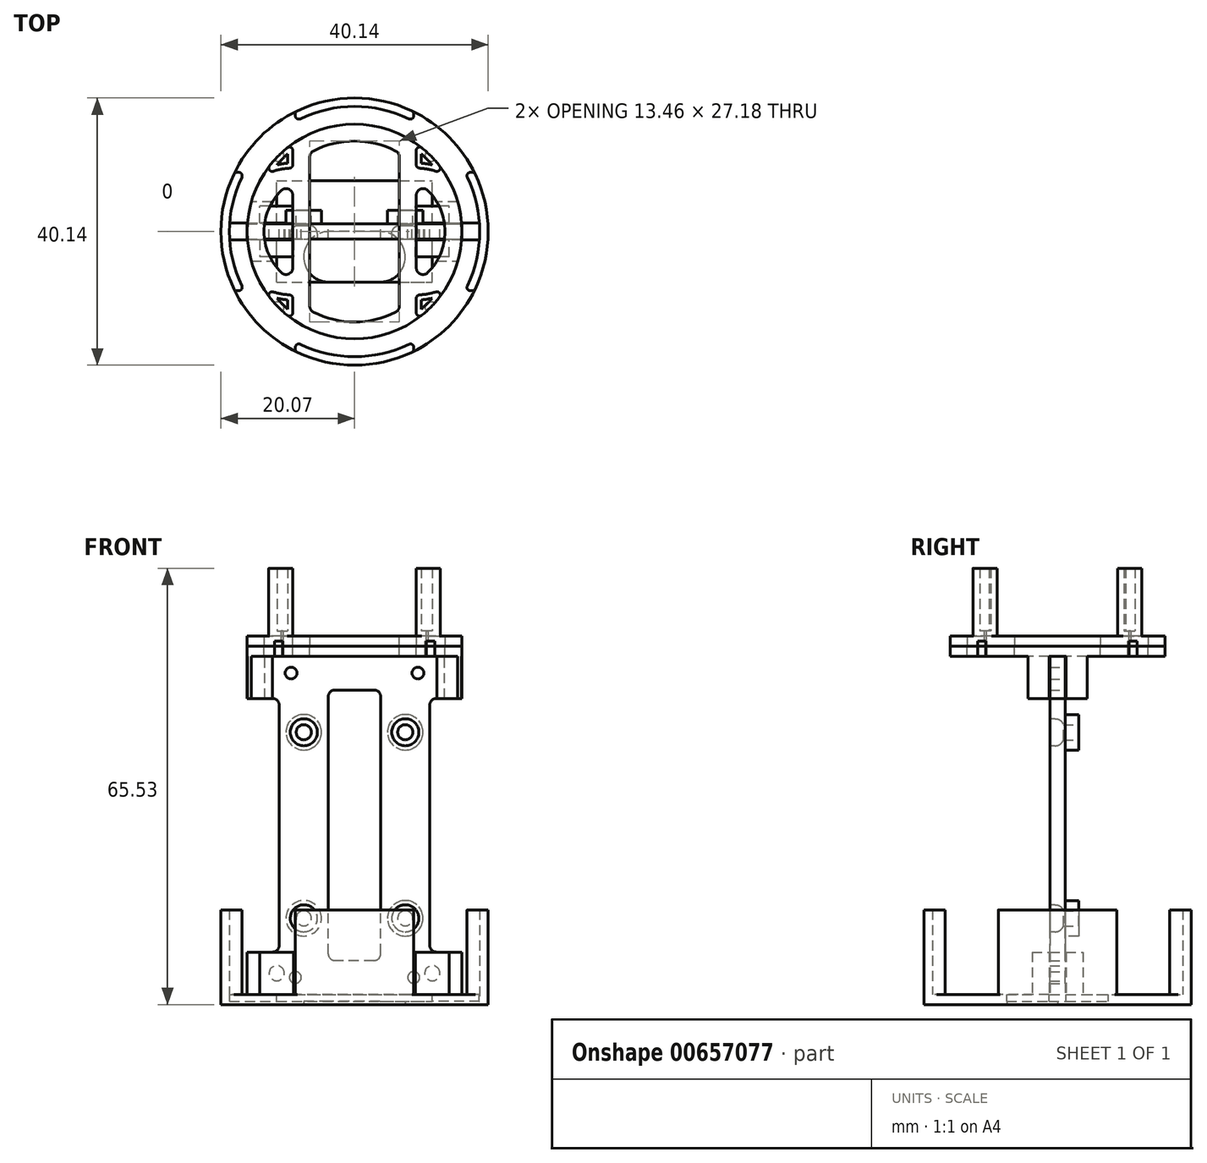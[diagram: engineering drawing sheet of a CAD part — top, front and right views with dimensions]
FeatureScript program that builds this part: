
annotation { "Feature Type Name" : "Feature", "Feature Type Description" : "" }
export const myFeature = defineFeature(function(context is Context, id is Id, definition is map)
    precondition{}
    {
        {
            var Q0;
            Q0=qCreatedBy(makeId("Top.planeOp"),FACE);
            var sketch = newSketch(context, id + "F0", { "sketchPlane" : qUnion([Q0])});
            skCircle(sketch, "E0", {"center": v(0, 0) * mm, "radius": 16.13 * mm});
            skSolve(sketch);
        }
        {
            var Q0;
            Q0=qSketchRegion(id+"F0",true);
            extrude(context, id + "F1", {"entities" : qUnion([Q0]), "depth" : 1.52 * mm, "offsetDistance" : 25.4 * mm});
        }
        {
            var Q0;
            Q0=makeQuery(id+"F1.opExtrude","CAP_FACE",FACE,{"disambiguationData":[OSD([sQuery(id+"F0.wireOp",EDGE,"E0")])],"isStart":false});
            var sketch = newSketch(context, id + "F2", { "sketchPlane" : qUnion([Q0])});
            skLineSegment(sketch, "E1.bottom", {"start": v(-9.27, 9.53) * mm, "end": v(9.27, 9.53) * mm, "construction": true});
            skLineSegment(sketch, "E1.top", {"start": v(-9.27, -9.53) * mm, "end": v(9.27, -9.53) * mm, "construction": true});
            skLineSegment(sketch, "E1.left", {"start": v(-9.27, 9.52) * mm, "end": v(-9.27, -9.53) * mm, "construction": true});
            skLineSegment(sketch, "E1.right", {"start": v(9.27, 9.53) * mm, "end": v(9.27, -9.53) * mm, "construction": true});
            skPoint(sketch, "E1.middle", {"position": v(0, 0) * mm});
            skArc(sketch, "E2", {"start": v(-9.27, 9.52) * mm, "mid": v(-11.6, 9.24) * mm, "end": v(-13.77, 8.4) * mm});
            skArc(sketch, "E3", {"start": v(9.27, -9.52) * mm, "mid": v(11.6, -9.24) * mm, "end": v(13.77, -8.4) * mm});
            skArc(sketch, "E4", {"start": v(-13.77, 8.4) * mm, "mid": v(-18.8, 0) * mm, "end": v(-13.77, -8.4) * mm, "construction": true});
            skArc(sketch, "E5", {"start": v(-13.77, 8.4) * mm, "mid": v(-16.13, 0) * mm, "end": v(-13.77, -8.4) * mm, "construction": true});
            skArc(sketch, "E6", {"start": v(-13.77, -8.4) * mm, "mid": v(0, -16.13) * mm, "end": v(13.77, -8.4) * mm});
            skArc(sketch, "E7", {"start": v(-13.77, -8.4) * mm, "mid": v(-11.6, -9.24) * mm, "end": v(-9.27, -9.53) * mm});
            skArc(sketch, "E8", {"start": v(13.77, 8.4) * mm, "mid": v(11.6, 9.24) * mm, "end": v(9.27, 9.53) * mm});
            skLineSegment(sketch, "E9", {"start": v(13.77, -8.4) * mm, "end": v(13.77, -8.4) * mm});
            skArc(sketch, "E10", {"start": v(13.77, -8.4) * mm, "mid": v(18.8, 0) * mm, "end": v(13.77, 8.4) * mm, "construction": true});
            skLineSegment(sketch, "E11", {"start": v(13.77, 8.4) * mm, "end": v(13.77, 8.4) * mm});
            skArc(sketch, "E12", {"start": v(13.77, 8.4) * mm, "mid": v(0, 16.13) * mm, "end": v(-13.77, 8.4) * mm});
            skArc(sketch, "E13", {"start": v(13.77, -8.4) * mm, "mid": v(16.13, 0) * mm, "end": v(13.77, 8.4) * mm, "construction": true});
            skLineSegment(sketch, "E14", {"start": v(-9.27, -9.53) * mm, "end": v(-9.27, -13.2) * mm});
            skLineSegment(sketch, "E15", {"start": v(9.27, -9.53) * mm, "end": v(9.27, -13.2) * mm});
            skLineSegment(sketch, "E16", {"start": v(9.27, 9.53) * mm, "end": v(9.27, 13.2) * mm});
            skLineSegment(sketch, "E17", {"start": v(-9.27, 9.53) * mm, "end": v(-9.27, 13.2) * mm});
            skArc(sketch, "E18", {"start": v(9.27, 13.2) * mm, "mid": v(0, 16.13) * mm, "end": v(-9.27, 13.2) * mm});
            skArc(sketch, "E19", {"start": v(-9.27, -13.2) * mm, "mid": v(0, -16.13) * mm, "end": v(9.27, -13.2) * mm});
            skSolve(sketch);
        }
        {
            var Q0;
            Q0=qSketchRegion(id+"F2",true);
            extrude(context, id + "F3", {"entities" : qUnion([Q0]), "operationType" : NewBodyOperationType.ADD, "depth" : 10.16 * mm, "offsetDistance" : 25.4 * mm});
        }
        {
            var Q0;
            Q0=makeQuery(id+"F3.opExtrude","SWEPT_EDGE",EDGE,{"disambiguationData":[OSD([sQuery(id+"F0.wireOp",EDGE,"E0"),sQuery(id+"F2.wireOp",EDGE,"E2"),sQuery(id+"F2.wireOp",EDGE,"E12")])]});
            var Q1;
            Q1=makeQuery(id+"F3.opExtrude","SWEPT_EDGE",EDGE,{"disambiguationData":[OSD([sQuery(id+"F0.wireOp",EDGE,"E0"),sQuery(id+"F2.wireOp",EDGE,"E6"),sQuery(id+"F2.wireOp",EDGE,"E7")])]});
            var Q2;
            Q2=makeQuery(id+"F3.opExtrude","SWEPT_EDGE",EDGE,{"disambiguationData":[OSD([sQuery(id+"F0.wireOp",EDGE,"E0"),sQuery(id+"F2.wireOp",EDGE,"E8"),sQuery(id+"F2.wireOp",EDGE,"E12")])]});
            var Q3;
            Q3=makeQuery(id+"F3.opExtrude","SWEPT_EDGE",EDGE,{"disambiguationData":[OSD([sQuery(id+"F0.wireOp",EDGE,"E0"),sQuery(id+"F2.wireOp",EDGE,"E3"),sQuery(id+"F2.wireOp",EDGE,"E6")])]});
            var Q4;
            Q4=makeQuery(id+"F3.opExtrude","SWEPT_EDGE",EDGE,{"disambiguationData":[OSD([sQuery(id+"F2.wireOp",EDGE,"E6"),sQuery(id+"F2.wireOp",EDGE,"E14"),sQuery(id+"F2.wireOp",EDGE,"E19")])]});
            var Q5;
            Q5=makeQuery(id+"F3.opExtrude","SWEPT_EDGE",EDGE,{"disambiguationData":[OSD([sQuery(id+"F0.wireOp",EDGE,"RRU1Pf1V-DoVO-Xhje-gmtz-4FpblWX3eckG.bottom"),sQuery(id+"F0.wireOp",EDGE,"RRU1Pf1V-DoVO-Xhje-gmtz-4FpblWX3eckG.left"),sQuery(id+"F2.wireOp",EDGE,"E7"),sQuery(id+"F2.wireOp",EDGE,"E14")])]});
            var Q6;
            Q6=makeQuery(id+"F3.opExtrude","SWEPT_EDGE",EDGE,{"disambiguationData":[OSD([sQuery(id+"F0.wireOp",EDGE,"RRU1Pf1V-DoVO-Xhje-gmtz-4FpblWX3eckG.top"),sQuery(id+"F0.wireOp",EDGE,"RRU1Pf1V-DoVO-Xhje-gmtz-4FpblWX3eckG.left"),sQuery(id+"F2.wireOp",EDGE,"E2"),sQuery(id+"F2.wireOp",EDGE,"E17")])]});
            var Q7;
            Q7=makeQuery(id+"F3.opExtrude","SWEPT_EDGE",EDGE,{"disambiguationData":[OSD([sQuery(id+"F2.wireOp",EDGE,"E12"),sQuery(id+"F2.wireOp",EDGE,"E17"),sQuery(id+"F2.wireOp",EDGE,"E18")])]});
            var Q8;
            Q8=makeQuery(id+"F3.opExtrude","SWEPT_EDGE",EDGE,{"disambiguationData":[OSD([sQuery(id+"F2.wireOp",EDGE,"E12"),sQuery(id+"F2.wireOp",EDGE,"E16"),sQuery(id+"F2.wireOp",EDGE,"E18")])]});
            var Q9;
            Q9=makeQuery(id+"F3.opExtrude","SWEPT_EDGE",EDGE,{"disambiguationData":[OSD([sQuery(id+"F2.wireOp",EDGE,"E6"),sQuery(id+"F2.wireOp",EDGE,"E15"),sQuery(id+"F2.wireOp",EDGE,"E19")])]});
            var Q10;
            Q10=makeQuery(id+"F3.opExtrude","SWEPT_EDGE",EDGE,{"disambiguationData":[OSD([sQuery(id+"F0.wireOp",EDGE,"RRU1Pf1V-DoVO-Xhje-gmtz-4FpblWX3eckG.top"),sQuery(id+"F0.wireOp",EDGE,"RRU1Pf1V-DoVO-Xhje-gmtz-4FpblWX3eckG.right"),sQuery(id+"F2.wireOp",EDGE,"E8"),sQuery(id+"F2.wireOp",EDGE,"E16")])]});
            var Q11;
            Q11=makeQuery(id+"F3.opExtrude","SWEPT_EDGE",EDGE,{"disambiguationData":[OSD([sQuery(id+"F0.wireOp",EDGE,"RRU1Pf1V-DoVO-Xhje-gmtz-4FpblWX3eckG.bottom"),sQuery(id+"F0.wireOp",EDGE,"RRU1Pf1V-DoVO-Xhje-gmtz-4FpblWX3eckG.right"),sQuery(id+"F2.wireOp",EDGE,"E3"),sQuery(id+"F2.wireOp",EDGE,"E15")])]});
            fillet(context, id + "F4", {"entities" : qUnion([Q0, Q1, Q2, Q3, Q4, Q5, Q6, Q7, Q8, Q9, Q10, Q11]), "radius" : 0.5 * mm, "tangentPropagation" : true, "allowEdgeOverflow" : false});
        }
        {
            var Q0;
            Q0=makeQuery(id+"F3.opExtrude","CAP_FACE",FACE,{"disambiguationData":[OSD([sQuery(id+"F2.wireOp",EDGE,"E1.bottom"),sQuery(id+"F2.wireOp",EDGE,"E2"),sQuery(id+"F2.wireOp",EDGE,"E8"),sQuery(id+"F2.wireOp",EDGE,"E12")])],"isStart":false});
            var Q1;
            Q1=makeQuery(id+"F3.opExtrude","CAP_FACE",FACE,{"disambiguationData":[OSD([sQuery(id+"F2.wireOp",EDGE,"E1.top"),sQuery(id+"F2.wireOp",EDGE,"E3"),sQuery(id+"F2.wireOp",EDGE,"E6"),sQuery(id+"F2.wireOp",EDGE,"E7")])],"isStart":false});
            shell(context, id + "F5", {"entities" : qUnion([Q0, Q1]), "thickness" : 0.76 * mm});
        }
        {
            var Q0;
            Q0=makeQuery(id+"F1.opExtrude","CAP_FACE",FACE,{"disambiguationData":[OSD([sQuery(id+"F0.wireOp",EDGE,"E0")])],"isStart":true});
            var sketch = newSketch(context, id + "F6", { "sketchPlane" : qUnion([Q0])});
            skLineSegment(sketch, "E20.bottom", {"start": v(6.73, -11.8) * mm, "end": v(-6.73, -11.8) * mm, "construction": true});
            skLineSegment(sketch, "E20.top", {"start": v(6.73, 11.8) * mm, "end": v(-6.73, 11.8) * mm, "construction": true});
            skLineSegment(sketch, "E20.left", {"start": v(6.73, -11.8) * mm, "end": v(6.73, 11.8) * mm});
            skLineSegment(sketch, "E20.right", {"start": v(-6.73, -11.8) * mm, "end": v(-6.73, 11.8) * mm});
            skPoint(sketch, "E20.middle", {"position": v(0, 0) * mm});
            skArc(sketch, "E21", {"start": v(-6.73, -11.8) * mm, "mid": v(0, -13.59) * mm, "end": v(6.73, -11.8) * mm});
            skArc(sketch, "E22", {"start": v(6.73, 11.8) * mm, "mid": v(0, 13.59) * mm, "end": v(-6.73, 11.8) * mm});
            skLineSegment(sketch, "E23", {"start": v(0, -13.59) * mm, "end": v(0, -16.13) * mm, "construction": true});
            skLineSegment(sketch, "E24", {"start": v(6.73, -11.8) * mm, "end": v(9.27, -11.8) * mm, "construction": true});
            skLineSegment(sketch, "E25", {"start": v(9.27, -7.48) * mm, "end": v(9.27, 7.48) * mm});
            skPoint(sketch, "E26", {"position": v(9.27, 0) * mm});
            skArc(sketch, "E27", {"start": v(9.27, -7.48) * mm, "mid": v(13.59, 0) * mm, "end": v(9.27, 7.48) * mm});
            skLineSegment(sketch, "E28", {"start": v(13.59, 0) * mm, "end": v(16.13, 0) * mm, "construction": true});
            skLineSegment(sketch, "E29", {"start": v(9.27, -7.48) * mm, "end": v(9.27, -10.02) * mm, "construction": true});
            skLineSegment(sketch, "E30", {"start": v(-9.27, -7.48) * mm, "end": v(-9.27, 7.48) * mm});
            skArc(sketch, "E31", {"start": v(-9.27, 7.48) * mm, "mid": v(-13.59, 0) * mm, "end": v(-9.27, -7.48) * mm});
            skLineSegment(sketch, "E32", {"start": v(-13.59, 0) * mm, "end": v(-16.13, 0) * mm, "construction": true});
            skSolve(sketch);
        }
        {
            var Q0;
            Q0=qSketchRegion(id+"F6",true);
            var Q1;
            Q1=makeQuery(id+"F1.opExtrude","CAP_FACE",FACE,{"disambiguationData":[OSD([sQuery(id+"F0.wireOp",EDGE,"E0")])],"isStart":false});
            extrude(context, id + "F7", {"entities" : qUnion([Q0]), "operationType" : NewBodyOperationType.REMOVE, "endBound" : BoundingType.UP_TO_SURFACE, "oppositeDirection" : true, "depth" : 25.4 * mm, "endBoundEntityFace" : qUnion([Q1]), "offsetDistance" : 25.4 * mm});
        }
        {
            var Q0;
            Q0=makeQuery(id+"F3.opExtrude","CAP_EDGE",EDGE,{"disambiguationData":[OSD([sQuery(id+"F2.wireOp",EDGE,"E2")])],"isStart":true});
            var Q1;
            Q1=makeQuery(id+"F3.opExtrude","CAP_EDGE",EDGE,{"disambiguationData":[OSD([sQuery(id+"F2.wireOp",EDGE,"E7")])],"isStart":true});
            var Q2;
            Q2=makeQuery(id+"F3.opExtrude","CAP_EDGE",EDGE,{"disambiguationData":[OSD([sQuery(id+"F2.wireOp",EDGE,"E3")])],"isStart":true});
            var Q3;
            Q3=makeQuery(id+"F3.opExtrude","CAP_EDGE",EDGE,{"disambiguationData":[OSD([sQuery(id+"F2.wireOp",EDGE,"E8")])],"isStart":true});
            var Q4;
            {var subQ0=sQuery(id+"F6.wireOp",EDGE,"E31");var subQ1=sQuery(id+"F6.wireOp",EDGE,"E30");Q4=makeQuery(id+"F7.boolean.opBoolean","COPY",EDGE,{"derivedFrom":makeQuery(id+"F7.opExtrude","SWEPT_EDGE",EDGE,{"disambiguationData":[OSD([subQ1,subQ0]),TDD([makeQuery(id+"F6.imprint","INTERSECT",VERTEX,{"disambiguationData":[OD(0.0)],"derivedFrom":[subQ1,subQ0]})])]})});}
            var Q5;
            Q5=makeQuery(id+"F7.boolean.opBoolean","COPY",EDGE,{"derivedFrom":makeQuery(id+"F7.opExtrude","SWEPT_EDGE",EDGE,{"disambiguationData":[OSD([sQuery(id+"F6.wireOp",EDGE,"E20.right"),sQuery(id+"F6.wireOp",EDGE,"E21")])]})});
            var Q6;
            Q6=makeQuery(id+"F7.boolean.opBoolean","COPY",EDGE,{"derivedFrom":makeQuery(id+"F7.opExtrude","SWEPT_EDGE",EDGE,{"disambiguationData":[OSD([sQuery(id+"F6.wireOp",EDGE,"E20.left"),sQuery(id+"F6.wireOp",EDGE,"E21")])]})});
            var Q7;
            {var subQ0=sQuery(id+"F6.wireOp",EDGE,"E31");var subQ1=sQuery(id+"F6.wireOp",EDGE,"E30");Q7=makeQuery(id+"F7.boolean.opBoolean","COPY",EDGE,{"derivedFrom":makeQuery(id+"F7.opExtrude","SWEPT_EDGE",EDGE,{"disambiguationData":[OSD([subQ1,subQ0]),TDD([makeQuery(id+"F6.imprint","INTERSECT",VERTEX,{"disambiguationData":[OD(1.0)],"derivedFrom":[subQ1,subQ0]})])]})});}
            var Q8;
            Q8=makeQuery(id+"F7.boolean.opBoolean","COPY",EDGE,{"derivedFrom":makeQuery(id+"F7.opExtrude","SWEPT_EDGE",EDGE,{"disambiguationData":[OSD([sQuery(id+"F6.wireOp",EDGE,"E20.left"),sQuery(id+"F6.wireOp",EDGE,"E22")])]})});
            var Q9;
            {var subQ0=sQuery(id+"F6.wireOp",EDGE,"E27");var subQ1=sQuery(id+"F6.wireOp",EDGE,"E25");Q9=makeQuery(id+"F7.boolean.opBoolean","COPY",EDGE,{"derivedFrom":makeQuery(id+"F7.opExtrude","SWEPT_EDGE",EDGE,{"disambiguationData":[OSD([subQ1,subQ0]),TDD([makeQuery(id+"F6.imprint","INTERSECT",VERTEX,{"disambiguationData":[OD(1.0)],"derivedFrom":[subQ1,subQ0]})])]})});}
            var Q10;
            Q10=makeQuery(id+"F7.boolean.opBoolean","COPY",EDGE,{"derivedFrom":makeQuery(id+"F7.opExtrude","SWEPT_EDGE",EDGE,{"disambiguationData":[OSD([sQuery(id+"F6.wireOp",EDGE,"E20.right"),sQuery(id+"F6.wireOp",EDGE,"E22")])]})});
            var Q11;
            {var subQ0=sQuery(id+"F6.wireOp",EDGE,"E27");var subQ1=sQuery(id+"F6.wireOp",EDGE,"E25");Q11=makeQuery(id+"F7.boolean.opBoolean","COPY",EDGE,{"derivedFrom":makeQuery(id+"F7.opExtrude","SWEPT_EDGE",EDGE,{"disambiguationData":[OSD([subQ1,subQ0]),TDD([makeQuery(id+"F6.imprint","INTERSECT",VERTEX,{"disambiguationData":[OD(0.0)],"derivedFrom":[subQ1,subQ0]})])]})});}
            fillet(context, id + "F8", {"entities" : qUnion([Q0, Q1, Q2, Q3, Q4, Q5, Q6, Q7, Q8, Q9, Q10, Q11]), "radius" : 1.02 * mm, "tangentPropagation" : true, "allowEdgeOverflow" : false});
        }
        {
            var Q0;
            Q0=makeQuery(id+"F5.opShell","OFFSET_FACE",FACE,{"disambiguationData":[OSD([sQuery(id+"F0.wireOp",EDGE,"E0")]),OD(0.0)]});
            var sketch = newSketch(context, id + "F9", { "sketchPlane" : qUnion([Q0])});
            skCircle(sketch, "E33", {"center": v(-11.5, 11.46) * mm, "radius": 0.89 * mm});
            skLineSegment(sketch, "E34.bottom", {"start": v(-11.5, 11.46) * mm, "end": v(11.5, 11.46) * mm, "construction": true});
            skLineSegment(sketch, "E34.top", {"start": v(-11.5, -11.46) * mm, "end": v(11.5, -11.46) * mm, "construction": true});
            skLineSegment(sketch, "E34.left", {"start": v(-11.5, 11.46) * mm, "end": v(-11.5, -11.46) * mm, "construction": true});
            skLineSegment(sketch, "E34.right", {"start": v(11.5, 11.46) * mm, "end": v(11.5, -11.46) * mm, "construction": true});
            skPoint(sketch, "E34.middle", {"position": v(0, 0) * mm});
            skCircle(sketch, "E35", {"center": v(11.5, 11.46) * mm, "radius": 0.89 * mm});
            skCircle(sketch, "E36", {"center": v(11.5, -11.46) * mm, "radius": 0.89 * mm});
            skCircle(sketch, "E37", {"center": v(-11.5, -11.46) * mm, "radius": 0.89 * mm});
            skSolve(sketch);
        }
        {
            var Q0;
            Q0=qSketchRegion(id+"F9",true);
            var Q1;
            Q1=makeQuery(id+"F1.opExtrude","CAP_FACE",FACE,{"disambiguationData":[OSD([sQuery(id+"F0.wireOp",EDGE,"E0")])],"isStart":true});
            extrude(context, id + "F10", {"entities" : qUnion([Q0]), "operationType" : NewBodyOperationType.REMOVE, "endBound" : BoundingType.UP_TO_SURFACE, "oppositeDirection" : true, "depth" : 25.4 * mm, "endBoundEntityFace" : qUnion([Q1]), "offsetDistance" : 25.4 * mm});
        }
        {
            var Q0;
            Q0=makeQuery(id+"F5.opShell","OFFSET_FACE",FACE,{"disambiguationData":[OSD([sQuery(id+"F0.wireOp",EDGE,"E0")]),OD(2.0)]});
            var Q1;
            Q1=makeQuery(id+"F5.opShell","OFFSET_FACE",FACE,{"disambiguationData":[OSD([sQuery(id+"F0.wireOp",EDGE,"E0")]),OD(1.0)]});
            var Q2;
            Q2=makeQuery(id+"F5.opShell","OFFSET_FACE",FACE,{"disambiguationData":[OSD([sQuery(id+"F0.wireOp",EDGE,"E0")]),OD(3.0)]});
            var Q3;
            Q3=makeQuery(id+"F5.opShell","OFFSET_FACE",FACE,{"disambiguationData":[OSD([sQuery(id+"F0.wireOp",EDGE,"E0")]),OD(0.0)]});
            extrude(context, id + "F11", {"entities" : qUnion([Q0, Q1, Q2, Q3]), "operationType" : NewBodyOperationType.ADD, "depth" : 1.52 * mm, "offsetDistance" : 25.4 * mm});
        }
        {
            var Q0;
            Q0=makeQuery(id+"F1.opExtrude","CAP_FACE",FACE,{"disambiguationData":[OSD([sQuery(id+"F0.wireOp",EDGE,"E0")])],"isStart":true});
            extrude(context, id + "F12", {"entities" : qUnion([Q0]), "depth" : 7.87 * mm, "offsetDistance" : 25.4 * mm});
        }
        {
            var Q0;
            Q0=makeQuery(id+"F12.opExtrude","CAP_FACE",FACE,{"disambiguationData":[OSD([sQuery(id+"F0.wireOp",EDGE,"E0")])],"isStart":false});
            var sketch = newSketch(context, id + "F13", { "sketchPlane" : qUnion([Q0])});
            skArc(sketch, "E38", {"start": v(-15.5, 4.44) * mm, "mid": v(-15.87, 2.87) * mm, "end": v(-16.08, 1.27) * mm, "construction": true});
            skArc(sketch, "E39", {"start": v(-15.5, -4.45) * mm, "mid": v(0, -16.13) * mm, "end": v(15.5, -4.45) * mm});
            skArc(sketch, "E40", {"start": v(15.5, -4.44) * mm, "mid": v(15.87, -2.87) * mm, "end": v(16.08, -1.27) * mm, "construction": true});
            skArc(sketch, "E41", {"start": v(15.5, 4.45) * mm, "mid": v(0, 16.13) * mm, "end": v(-15.5, 4.45) * mm});
            skLineSegment(sketch, "E42", {"start": v(-15.5, 4.45) * mm, "end": v(-9.27, 4.45) * mm});
            skLineSegment(sketch, "E43", {"start": v(15.5, -4.45) * mm, "end": v(9.27, -4.45) * mm});
            skArc(sketch, "E44", {"start": v(-16.08, 1.27) * mm, "mid": v(-16.13, 0) * mm, "end": v(-16.08, -1.27) * mm});
            skArc(sketch, "E45", {"start": v(-16.08, -1.27) * mm, "mid": v(-15.87, -2.87) * mm, "end": v(-15.5, -4.44) * mm, "construction": true});
            skArc(sketch, "E46", {"start": v(16.08, -1.27) * mm, "mid": v(16.13, 0) * mm, "end": v(16.08, 1.27) * mm});
            skArc(sketch, "E47", {"start": v(16.08, 1.27) * mm, "mid": v(15.87, 2.87) * mm, "end": v(15.5, 4.44) * mm, "construction": true});
            skLineSegment(sketch, "E48", {"start": v(16.08, 1.27) * mm, "end": v(9.27, 1.27) * mm});
            skLineSegment(sketch, "E49", {"start": v(-16.08, -1.27) * mm, "end": v(-9.27, -1.27) * mm});
            skLineSegment(sketch, "E50", {"start": v(-9.27, 4.45) * mm, "end": v(9.27, 4.45) * mm, "construction": true});
            skLineSegment(sketch, "E51", {"start": v(-9.27, 1.27) * mm, "end": v(-16.08, 1.27) * mm});
            skLineSegment(sketch, "E52", {"start": v(-9.27, -1.27) * mm, "end": v(9.27, -1.27) * mm, "construction": true});
            skLineSegment(sketch, "E53", {"start": v(-9.27, -4.45) * mm, "end": v(-15.5, -4.45) * mm});
            skLineSegment(sketch, "E54", {"start": v(9.27, -4.45) * mm, "end": v(-9.27, -4.45) * mm, "construction": true});
            skLineSegment(sketch, "E55", {"start": v(9.27, -1.27) * mm, "end": v(16.08, -1.27) * mm});
            skLineSegment(sketch, "E56", {"start": v(9.27, 1.27) * mm, "end": v(-9.27, 1.27) * mm, "construction": true});
            skLineSegment(sketch, "E57", {"start": v(9.27, 4.45) * mm, "end": v(15.5, 4.45) * mm});
            skLineSegment(sketch, "E58", {"start": v(0, 1.27) * mm, "end": v(0, -1.27) * mm, "construction": true});
            skLineSegment(sketch, "E59", {"start": v(0, 4.45) * mm, "end": v(0, -4.45) * mm, "construction": true});
            skLineSegment(sketch, "E60", {"start": v(-9.27, 4.45) * mm, "end": v(-9.27, 1.27) * mm});
            skLineSegment(sketch, "E61", {"start": v(-9.27, -1.27) * mm, "end": v(-9.27, -4.45) * mm});
            skLineSegment(sketch, "E62", {"start": v(9.27, -4.45) * mm, "end": v(9.27, -1.27) * mm});
            skLineSegment(sketch, "E63", {"start": v(9.27, 1.27) * mm, "end": v(9.27, 4.45) * mm});
            skSolve(sketch);
        }
        {
            var Q0;
            Q0=qSketchRegion(id+"F13",true);
            extrude(context, id + "F14", {"entities" : qUnion([Q0]), "operationType" : NewBodyOperationType.REMOVE, "oppositeDirection" : true, "depth" : 6.35 * mm, "offsetDistance" : 25.4 * mm});
        }
        {
            var Q0;
            Q0=qCreatedBy(makeId("Front.planeOp"),FACE);
            var sketch = newSketch(context, id + "F15", { "sketchPlane" : qUnion([Q0])});
            skLineSegment(sketch, "E64.bottom", {"start": v(-7.62, -40.9) * mm, "end": v(7.62, -40.9) * mm, "construction": true});
            skLineSegment(sketch, "E64.top", {"start": v(-7.62, -12.95) * mm, "end": v(7.62, -12.95) * mm, "construction": true});
            skLineSegment(sketch, "E64.left", {"start": v(-7.62, -40.9) * mm, "end": v(-7.62, -12.95) * mm, "construction": true});
            skLineSegment(sketch, "E64.right", {"start": v(7.62, -40.9) * mm, "end": v(7.62, -12.95) * mm, "construction": true});
            skPoint(sketch, "E64.middle", {"position": v(0, -26.92) * mm});
            skCircle(sketch, "E65", {"center": v(-7.62, -40.9) * mm, "radius": 1.14 * mm});
            skCircle(sketch, "E66", {"center": v(-7.62, -12.95) * mm, "radius": 1.14 * mm});
            skCircle(sketch, "E67", {"center": v(7.62, -12.95) * mm, "radius": 1.14 * mm});
            skCircle(sketch, "E68", {"center": v(7.62, -40.9) * mm, "radius": 1.14 * mm});
            skLineSegment(sketch, "E69", {"start": v(-8.89, -49.78) * mm, "end": v(8.89, -49.78) * mm, "construction": true});
            skLineSegment(sketch, "E70", {"start": v(-9.53, -4.06) * mm, "end": v(9.53, -4.06) * mm, "construction": true});
            skPoint(sketch, "E71", {"position": v(0, -49.78) * mm});
            skPoint(sketch, "E72", {"position": v(0, -4.06) * mm});
            skLineSegment(sketch, "E73", {"start": v(0, -49.78) * mm, "end": v(0, -4.06) * mm, "construction": true});
            skCircle(sketch, "E74", {"center": v(-8.89, -49.78) * mm, "radius": 0.89 * mm});
            skCircle(sketch, "E75", {"center": v(8.89, -49.78) * mm, "radius": 0.89 * mm});
            skCircle(sketch, "E76", {"center": v(9.53, -4.06) * mm, "radius": 0.89 * mm});
            skCircle(sketch, "E77", {"center": v(-9.53, -4.06) * mm, "radius": 0.89 * mm});
            skLineSegment(sketch, "E78", {"start": v(-16.13, -52.32) * mm, "end": v(16.13, -52.32) * mm});
            skPoint(sketch, "E79", {"position": v(0, -52.32) * mm});
            skLineSegment(sketch, "E80", {"start": v(-16.13, -1.52) * mm, "end": v(16.13, -1.52) * mm});
            skLineSegment(sketch, "E81", {"start": v(9.52, -4.06) * mm, "end": v(9.52, -1.52) * mm, "construction": true});
            skLineSegment(sketch, "E82", {"start": v(8.9, -49.78) * mm, "end": v(8.9, -52.32) * mm, "construction": true});
            skLineSegment(sketch, "E83", {"start": v(-16.13, -1.52) * mm, "end": v(-16.13, -7.87) * mm});
            skLineSegment(sketch, "E84", {"start": v(-16.13, -7.87) * mm, "end": v(-11.3, -7.87) * mm});
            skLineSegment(sketch, "E85", {"start": v(-11.3, -7.87) * mm, "end": v(-11.3, -45.97) * mm});
            skLineSegment(sketch, "E86", {"start": v(-11.3, -45.97) * mm, "end": v(-16.13, -45.97) * mm});
            skLineSegment(sketch, "E87", {"start": v(-16.13, -45.97) * mm, "end": v(-16.13, -52.32) * mm});
            skLineSegment(sketch, "E88", {"start": v(16.13, -1.52) * mm, "end": v(16.13, -7.87) * mm});
            skLineSegment(sketch, "E89", {"start": v(16.13, -7.87) * mm, "end": v(11.3, -7.87) * mm});
            skLineSegment(sketch, "E90", {"start": v(11.3, -7.87) * mm, "end": v(11.3, -45.97) * mm});
            skLineSegment(sketch, "E91", {"start": v(11.3, -45.97) * mm, "end": v(16.13, -45.97) * mm});
            skLineSegment(sketch, "E92", {"start": v(16.13, -45.97) * mm, "end": v(16.13, -52.32) * mm});
            skLineSegment(sketch, "E93", {"start": v(-8.76, -40.9) * mm, "end": v(-11.3, -40.9) * mm, "construction": true});
            skLineSegment(sketch, "E94.bottom", {"start": v(3.94, -47.24) * mm, "end": v(-3.94, -47.24) * mm});
            skLineSegment(sketch, "E94.top", {"start": v(3.94, -6.6) * mm, "end": v(-3.94, -6.6) * mm});
            skLineSegment(sketch, "E94.left", {"start": v(3.94, -47.24) * mm, "end": v(3.94, -6.6) * mm});
            skLineSegment(sketch, "E94.right", {"start": v(-3.94, -47.24) * mm, "end": v(-3.94, -6.6) * mm});
            skLineSegment(sketch, "E95", {"start": v(-6.48, -40.9) * mm, "end": v(-3.94, -40.9) * mm, "construction": true});
            skLineSegment(sketch, "E96", {"start": v(0, -49.78) * mm, "end": v(0, -47.24) * mm, "construction": true});
            skCircle(sketch, "E97", {"center": v(-11.68, -49.15) * mm, "radius": 1.14 * mm});
            skPoint(sketch, "E97.centerSnap0", {"position": v(-16.13, -49.15) * mm});
            skCircle(sketch, "E98", {"center": v(11.68, -49.15) * mm, "radius": 1.14 * mm});
            skPoint(sketch, "E98.centerSnap0", {"position": v(16.13, -49.15) * mm});
            skLineSegment(sketch, "E99", {"start": v(-11.68, -49.15) * mm, "end": v(-16.13, -49.15) * mm, "construction": true});
            skLineSegment(sketch, "E100", {"start": v(11.68, -49.15) * mm, "end": v(16.13, -49.15) * mm, "construction": true});
            skSolve(sketch);
        }
        {
            var Q0;
            Q0=qSketchRegion(id+"F15",true);
            extrude(context, id + "F16", {"entities" : qUnion([Q0]), "endBound" : BoundingType.SYMMETRIC, "depth" : 2.3 * mm, "offsetDistance" : 25.4 * mm});
        }
        {
            var Q0;
            Q0=makeQuery(id+"F16.opExtrude","CAP_FACE",FACE,{"disambiguationData":[OSD([sQuery(id+"F15.wireOp",EDGE,"E65"),sQuery(id+"F15.wireOp",EDGE,"E66"),sQuery(id+"F15.wireOp",EDGE,"E67"),sQuery(id+"F15.wireOp",EDGE,"E68"),sQuery(id+"F15.wireOp",EDGE,"E74"),sQuery(id+"F15.wireOp",EDGE,"E75"),sQuery(id+"F15.wireOp",EDGE,"E76"),sQuery(id+"F15.wireOp",EDGE,"E77"),sQuery(id+"F15.wireOp",EDGE,"E78"),sQuery(id+"F15.wireOp",EDGE,"E80"),sQuery(id+"F15.wireOp",EDGE,"E83"),sQuery(id+"F15.wireOp",EDGE,"E84"),sQuery(id+"F15.wireOp",EDGE,"E85"),sQuery(id+"F15.wireOp",EDGE,"E86"),sQuery(id+"F15.wireOp",EDGE,"E87"),sQuery(id+"F15.wireOp",EDGE,"E88"),sQuery(id+"F15.wireOp",EDGE,"E89"),sQuery(id+"F15.wireOp",EDGE,"E90"),sQuery(id+"F15.wireOp",EDGE,"E91"),sQuery(id+"F15.wireOp",EDGE,"E92"),sQuery(id+"F15.wireOp",EDGE,"E94.bottom"),sQuery(id+"F15.wireOp",EDGE,"E94.top"),sQuery(id+"F15.wireOp",EDGE,"E94.left"),sQuery(id+"F15.wireOp",EDGE,"E94.right")])],"isStart":true});
            var sketch = newSketch(context, id + "F17", { "sketchPlane" : qUnion([Q0])});
            skCircle(sketch, "E101", {"center": v(7.62, -40.9) * mm, "radius": 1.14 * mm});
            skCircle(sketch, "E102", {"center": v(-7.62, -40.9) * mm, "radius": 1.14 * mm});
            skCircle(sketch, "E103", {"center": v(-7.62, -12.95) * mm, "radius": 1.14 * mm});
            skCircle(sketch, "E104", {"center": v(7.62, -12.95) * mm, "radius": 1.14 * mm});
            skCircle(sketch, "E105", {"center": v(7.62, -40.9) * mm, "radius": 2.67 * mm});
            skCircle(sketch, "E106", {"center": v(-7.62, -40.9) * mm, "radius": 2.67 * mm});
            skCircle(sketch, "E107", {"center": v(-7.62, -12.95) * mm, "radius": 2.67 * mm});
            skCircle(sketch, "E108", {"center": v(7.62, -12.95) * mm, "radius": 2.67 * mm});
            skSolve(sketch);
        }
        {
            var Q0;
            Q0=qSketchRegion(id+"F17",true);
            extrude(context, id + "F18", {"entities" : qUnion([Q0]), "operationType" : NewBodyOperationType.ADD, "depth" : 2.03 * mm, "offsetDistance" : 25.4 * mm});
        }
        {
            var Q0;
            Q0=makeQuery(id+"F18.opExtrude","CAP_EDGE",EDGE,{"disambiguationData":[OSD([sQuery(id+"F17.wireOp",EDGE,"E105")])],"isStart":true});
            var Q1;
            Q1=makeQuery(id+"F18.opExtrude","CAP_EDGE",EDGE,{"disambiguationData":[OSD([sQuery(id+"F17.wireOp",EDGE,"E106")])],"isStart":true});
            var Q2;
            Q2=makeQuery(id+"F18.opExtrude","CAP_EDGE",EDGE,{"disambiguationData":[OSD([sQuery(id+"F17.wireOp",EDGE,"E108")])],"isStart":true});
            var Q3;
            Q3=makeQuery(id+"F18.opExtrude","CAP_EDGE",EDGE,{"disambiguationData":[OSD([sQuery(id+"F17.wireOp",EDGE,"E107")])],"isStart":true});
            var Q4;
            Q4=makeQuery(id+"F16.opExtrude","SWEPT_EDGE",EDGE,{"disambiguationData":[OSD([sQuery(id+"F15.wireOp",EDGE,"E85"),sQuery(id+"F15.wireOp",EDGE,"E86")])]});
            var Q5;
            Q5=makeQuery(id+"F16.opExtrude","SWEPT_EDGE",EDGE,{"disambiguationData":[OSD([sQuery(id+"F15.wireOp",EDGE,"E94.bottom"),sQuery(id+"F15.wireOp",EDGE,"E94.left")])]});
            var Q6;
            Q6=makeQuery(id+"F16.opExtrude","SWEPT_EDGE",EDGE,{"disambiguationData":[OSD([sQuery(id+"F15.wireOp",EDGE,"E94.bottom"),sQuery(id+"F15.wireOp",EDGE,"E94.right")])]});
            var Q7;
            Q7=makeQuery(id+"F16.opExtrude","SWEPT_EDGE",EDGE,{"disambiguationData":[OSD([sQuery(id+"F15.wireOp",EDGE,"E90"),sQuery(id+"F15.wireOp",EDGE,"E91")])]});
            var Q8;
            Q8=makeQuery(id+"F16.opExtrude","SWEPT_EDGE",EDGE,{"disambiguationData":[OSD([sQuery(id+"F15.wireOp",EDGE,"E84"),sQuery(id+"F15.wireOp",EDGE,"E85")])]});
            var Q9;
            Q9=makeQuery(id+"F16.opExtrude","SWEPT_EDGE",EDGE,{"disambiguationData":[OSD([sQuery(id+"F15.wireOp",EDGE,"E94.top"),sQuery(id+"F15.wireOp",EDGE,"E94.left")])]});
            var Q10;
            Q10=makeQuery(id+"F16.opExtrude","SWEPT_EDGE",EDGE,{"disambiguationData":[OSD([sQuery(id+"F15.wireOp",EDGE,"E94.top"),sQuery(id+"F15.wireOp",EDGE,"E94.right")])]});
            var Q11;
            Q11=makeQuery(id+"F16.opExtrude","SWEPT_EDGE",EDGE,{"disambiguationData":[OSD([sQuery(id+"F15.wireOp",EDGE,"E89"),sQuery(id+"F15.wireOp",EDGE,"E90")])]});
            fillet(context, id + "F19", {"entities" : qUnion([Q0, Q1, Q2, Q3, Q4, Q5, Q6, Q7, Q8, Q9, Q10, Q11]), "radius" : 1.02 * mm, "tangentPropagation" : true, "allowEdgeOverflow" : false});
        }
        {
            var Q0;
            Q0=makeQuery(id+"F16.opExtrude","CAP_FACE",FACE,{"disambiguationData":[OSD([sQuery(id+"F15.wireOp",EDGE,"E65"),sQuery(id+"F15.wireOp",EDGE,"E66"),sQuery(id+"F15.wireOp",EDGE,"E67"),sQuery(id+"F15.wireOp",EDGE,"E68"),sQuery(id+"F15.wireOp",EDGE,"E74"),sQuery(id+"F15.wireOp",EDGE,"E75"),sQuery(id+"F15.wireOp",EDGE,"E76"),sQuery(id+"F15.wireOp",EDGE,"E77"),sQuery(id+"F15.wireOp",EDGE,"E78"),sQuery(id+"F15.wireOp",EDGE,"E80"),sQuery(id+"F15.wireOp",EDGE,"E83"),sQuery(id+"F15.wireOp",EDGE,"E84"),sQuery(id+"F15.wireOp",EDGE,"E85"),sQuery(id+"F15.wireOp",EDGE,"E86"),sQuery(id+"F15.wireOp",EDGE,"E87"),sQuery(id+"F15.wireOp",EDGE,"E88"),sQuery(id+"F15.wireOp",EDGE,"E89"),sQuery(id+"F15.wireOp",EDGE,"E90"),sQuery(id+"F15.wireOp",EDGE,"E91"),sQuery(id+"F15.wireOp",EDGE,"E92"),sQuery(id+"F15.wireOp",EDGE,"E94.bottom"),sQuery(id+"F15.wireOp",EDGE,"E94.top"),sQuery(id+"F15.wireOp",EDGE,"E94.left"),sQuery(id+"F15.wireOp",EDGE,"E94.right"),sQuery(id+"F15.wireOp",EDGE,"E97"),sQuery(id+"F15.wireOp",EDGE,"E98")])],"isStart":false});
            var sketch = newSketch(context, id + "F20", { "sketchPlane" : qUnion([Q0])});
            skCircle(sketch, "E109", {"center": v(-7.62, -40.9) * mm, "radius": 2.03 * mm});
            skCircle(sketch, "E110", {"center": v(-7.62, -12.95) * mm, "radius": 2.03 * mm});
            skCircle(sketch, "E111", {"center": v(7.62, -12.95) * mm, "radius": 2.03 * mm});
            skCircle(sketch, "E112", {"center": v(7.62, -40.9) * mm, "radius": 2.03 * mm});
            skSolve(sketch);
        }
        {
            var Q0;
            Q0=qSketchRegion(id+"F20",true);
            extrude(context, id + "F21", {"entities" : qUnion([Q0]), "operationType" : NewBodyOperationType.REMOVE, "oppositeDirection" : true, "depth" : 2.03 * mm, "offsetDistance" : 25.4 * mm});
        }
        {
            var Q0;
            Q0=makeQuery(id+"F21.boolean.opBoolean","COPY",EDGE,{"derivedFrom":makeQuery(id+"F21.opExtrude","CAP_EDGE",EDGE,{"disambiguationData":[OSD([sQuery(id+"F20.wireOp",EDGE,"E109")])],"isStart":false})});
            var Q1;
            Q1=makeQuery(id+"F21.boolean.opBoolean","COPY",EDGE,{"derivedFrom":makeQuery(id+"F21.opExtrude","CAP_EDGE",EDGE,{"disambiguationData":[OSD([sQuery(id+"F20.wireOp",EDGE,"E110")])],"isStart":false})});
            var Q2;
            Q2=makeQuery(id+"F21.boolean.opBoolean","COPY",EDGE,{"derivedFrom":makeQuery(id+"F21.opExtrude","CAP_EDGE",EDGE,{"disambiguationData":[OSD([sQuery(id+"F20.wireOp",EDGE,"E111")])],"isStart":false})});
            var Q3;
            Q3=makeQuery(id+"F21.boolean.opBoolean","COPY",EDGE,{"derivedFrom":makeQuery(id+"F21.opExtrude","CAP_EDGE",EDGE,{"disambiguationData":[OSD([sQuery(id+"F20.wireOp",EDGE,"E112")])],"isStart":false})});
            fillet(context, id + "F22", {"entities" : qUnion([Q0, Q1, Q2, Q3]), "radius" : 1.27 * mm, "tangentPropagation" : true, "allowEdgeOverflow" : false});
        }
        {
            var Q0;
            Q0=makeQuery(id+"F16.opExtrude","SWEPT_FACE",FACE,{"disambiguationData":[OSD([sQuery(id+"F15.wireOp",EDGE,"E78")])]});
            var sketch = newSketch(context, id + "F23", { "sketchPlane" : qUnion([Q0])});
            skCircle(sketch, "E113", {"center": v(0, 0) * mm, "radius": 20.07 * mm});
            skSolve(sketch);
        }
        {
            var Q0;
            Q0=qSketchRegion(id+"F23",true);
            extrude(context, id + "F24", {"entities" : qUnion([Q0]), "depth" : 1.52 * mm, "offsetDistance" : 25.4 * mm});
        }
        {
            var Q0;
            Q0=makeQuery(id+"F24.opExtrude","CAP_FACE",FACE,{"disambiguationData":[OSD([sQuery(id+"F23.wireOp",EDGE,"E113")])],"isStart":false});
            var sketch = newSketch(context, id + "F25", { "sketchPlane" : qUnion([Q0])});
            skLineSegment(sketch, "E114.bottom", {"start": v(3.8, 0) * mm, "end": v(-3.8, 0) * mm});
            skLineSegment(sketch, "E114.top", {"start": v(3.8, 7.62) * mm, "end": v(-3.8, 7.62) * mm});
            skLineSegment(sketch, "E114.left", {"start": v(3.8, 0) * mm, "end": v(3.8, 7.62) * mm});
            skLineSegment(sketch, "E114.right", {"start": v(-3.81, 0) * mm, "end": v(-3.81, 7.62) * mm});
            skArc(sketch, "E115", {"start": v(3.81, 0) * mm, "mid": v(7.62, 3.81) * mm, "end": v(3.8, 7.62) * mm});
            skArc(sketch, "E116", {"start": v(-3.81, 7.62) * mm, "mid": v(-7.62, 3.81) * mm, "end": v(-3.81, 0) * mm});
            skPoint(sketch, "E117", {"position": v(0, 0) * mm});
            skSolve(sketch);
        }
        {
            var Q0;
            Q0=qSketchRegion(id+"F25",true);
            var Q1;
            Q1=makeQuery(id+"F24.opExtrude","CAP_FACE",FACE,{"disambiguationData":[OSD([sQuery(id+"F23.wireOp",EDGE,"E113")])],"isStart":true});
            extrude(context, id + "F26", {"entities" : qUnion([Q0]), "operationType" : NewBodyOperationType.REMOVE, "endBound" : BoundingType.UP_TO_SURFACE, "oppositeDirection" : true, "depth" : 25.4 * mm, "endBoundEntityFace" : qUnion([Q1]), "offsetDistance" : 25.4 * mm});
        }
        {
            var Q0;
            Q0=makeQuery(id+"F24.opExtrude","CAP_FACE",FACE,{"disambiguationData":[OSD([sQuery(id+"F23.wireOp",EDGE,"E113")])],"isStart":true});
            var sketch = newSketch(context, id + "F27", { "sketchPlane" : qUnion([Q0])});
            skLineSegment(sketch, "E118.bottom", {"start": v(14.22, -3.8) * mm, "end": v(9.14, -3.81) * mm});
            skLineSegment(sketch, "E118.top", {"start": v(14.22, -1.27) * mm, "end": v(9.14, -1.27) * mm});
            skLineSegment(sketch, "E118.left", {"start": v(14.22, -3.81) * mm, "end": v(14.22, -1.27) * mm});
            skLineSegment(sketch, "E118.right", {"start": v(9.14, -3.81) * mm, "end": v(9.14, -1.27) * mm});
            skLineSegment(sketch, "E119.bottom", {"start": v(-9.14, 1.27) * mm, "end": v(-14.22, 1.27) * mm});
            skLineSegment(sketch, "E119.top", {"start": v(-9.14, 3.81) * mm, "end": v(-14.22, 3.81) * mm});
            skLineSegment(sketch, "E119.left", {"start": v(-9.14, 1.27) * mm, "end": v(-9.14, 3.81) * mm});
            skLineSegment(sketch, "E119.right", {"start": v(-14.22, 1.27) * mm, "end": v(-14.22, 3.81) * mm});
            skPoint(sketch, "E120", {"position": v(-11.68, 1.27) * mm});
            skPoint(sketch, "E121", {"position": v(-16.13, 1.14) * mm});
            skPoint(sketch, "E122", {"position": v(-20.07, 0) * mm});
            skPoint(sketch, "E123", {"position": v(20.07, 0) * mm});
            skPoint(sketch, "E124", {"position": v(16.13, -1.14) * mm});
            skPoint(sketch, "E125", {"position": v(11.68, -1.27) * mm});
            skLineSegment(sketch, "E126.bottom", {"start": v(14.22, 1.27) * mm, "end": v(9.14, 1.27) * mm});
            skLineSegment(sketch, "E126.top", {"start": v(14.22, 3.81) * mm, "end": v(9.14, 3.81) * mm});
            skLineSegment(sketch, "E126.left", {"start": v(14.22, 1.27) * mm, "end": v(14.22, 3.81) * mm});
            skLineSegment(sketch, "E126.right", {"start": v(9.14, 1.27) * mm, "end": v(9.14, 3.81) * mm});
            skLineSegment(sketch, "E127.bottom", {"start": v(-9.14, -1.27) * mm, "end": v(-14.22, -1.27) * mm});
            skLineSegment(sketch, "E127.top", {"start": v(-9.14, -3.8) * mm, "end": v(-14.22, -3.8) * mm});
            skLineSegment(sketch, "E127.left", {"start": v(-9.14, -1.27) * mm, "end": v(-9.14, -3.81) * mm});
            skLineSegment(sketch, "E127.right", {"start": v(-14.22, -1.27) * mm, "end": v(-14.22, -3.81) * mm});
            skSolve(sketch);
        }
        {
            var Q0;
            Q0=makeQuery(id+"F24.opExtrude","CAP_FACE",FACE,{"disambiguationData":[OSD([sQuery(id+"F23.wireOp",EDGE,"E113")])],"isStart":true});
            var sketch = newSketch(context, id + "F28", { "sketchPlane" : qUnion([Q0])});
            skLineSegment(sketch, "E128", {"start": v(0, -18.8) * mm, "end": v(0, -20.07) * mm, "construction": true});
            skArc(sketch, "E129", {"start": v(8.89, 17.99) * mm, "mid": v(0, 20.07) * mm, "end": v(-8.89, 17.99) * mm});
            skArc(sketch, "E130", {"start": v(-8.89, 17.99) * mm, "mid": v(-14.19, 14.19) * mm, "end": v(-17.99, 8.89) * mm, "construction": true});
            skArc(sketch, "E131", {"start": v(-8.9, 16.56) * mm, "mid": v(-13.3, 13.3) * mm, "end": v(-16.56, 8.89) * mm, "construction": true});
            skArc(sketch, "E132", {"start": v(8.9, 16.56) * mm, "mid": v(0, 18.8) * mm, "end": v(-8.9, 16.56) * mm});
            skArc(sketch, "E133", {"start": v(-8.9, -16.56) * mm, "mid": v(0, -18.8) * mm, "end": v(8.9, -16.56) * mm});
            skArc(sketch, "E134", {"start": v(8.9, -16.56) * mm, "mid": v(13.3, -13.3) * mm, "end": v(16.56, -8.89) * mm, "construction": true});
            skArc(sketch, "E135", {"start": v(8.89, -17.99) * mm, "mid": v(14.19, -14.19) * mm, "end": v(17.99, -8.89) * mm, "construction": true});
            skArc(sketch, "E136", {"start": v(-8.89, -17.99) * mm, "mid": v(0, -20.07) * mm, "end": v(8.89, -17.99) * mm});
            skLineSegment(sketch, "E137", {"start": v(8.89, 16.56) * mm, "end": v(8.89, 17.99) * mm});
            skLineSegment(sketch, "E138", {"start": v(-8.9, 17.99) * mm, "end": v(-8.9, 16.56) * mm});
            skLineSegment(sketch, "E139", {"start": v(-8.89, -16.56) * mm, "end": v(-8.89, -17.99) * mm});
            skLineSegment(sketch, "E140", {"start": v(8.89, -16.56) * mm, "end": v(8.9, -17.99) * mm});
            skArc(sketch, "E141", {"start": v(16.56, 8.89) * mm, "mid": v(13.3, 13.3) * mm, "end": v(8.9, 16.56) * mm, "construction": true});
            skArc(sketch, "E142", {"start": v(17.99, 8.89) * mm, "mid": v(14.19, 14.19) * mm, "end": v(8.89, 17.99) * mm, "construction": true});
            skArc(sketch, "E143", {"start": v(16.56, -8.89) * mm, "mid": v(18.8, 0) * mm, "end": v(16.56, 8.89) * mm});
            skArc(sketch, "E144", {"start": v(17.99, -8.89) * mm, "mid": v(20.07, 0) * mm, "end": v(17.99, 8.89) * mm});
            skArc(sketch, "E145", {"start": v(-16.56, 8.89) * mm, "mid": v(-18.8, 0) * mm, "end": v(-16.56, -8.89) * mm});
            skArc(sketch, "E146", {"start": v(-17.99, 8.89) * mm, "mid": v(-20.07, 0) * mm, "end": v(-17.99, -8.89) * mm});
            skArc(sketch, "E147", {"start": v(-16.56, -8.89) * mm, "mid": v(-13.3, -13.3) * mm, "end": v(-8.9, -16.56) * mm, "construction": true});
            skArc(sketch, "E148", {"start": v(-17.99, -8.89) * mm, "mid": v(-14.19, -14.19) * mm, "end": v(-8.89, -17.99) * mm, "construction": true});
            skLineSegment(sketch, "E149", {"start": v(-16.56, -8.9) * mm, "end": v(-17.99, -8.9) * mm});
            skLineSegment(sketch, "E150", {"start": v(-16.56, 8.89) * mm, "end": v(-17.99, 8.89) * mm});
            skLineSegment(sketch, "E151", {"start": v(17.99, 8.9) * mm, "end": v(16.56, 8.9) * mm});
            skLineSegment(sketch, "E152", {"start": v(17.99, -8.9) * mm, "end": v(16.56, -8.9) * mm});
            skSolve(sketch);
        }
        {
            var Q0;
            Q0=qSketchRegion(id+"F28",true);
            extrude(context, id + "F29", {"entities" : qUnion([Q0]), "operationType" : NewBodyOperationType.ADD, "depth" : 12.7 * mm, "offsetDistance" : 25.4 * mm});
        }
        {
            var Q0;
            Q0=makeQuery(id+"F29.opExtrude","SWEPT_EDGE",EDGE,{"disambiguationData":[OSD([sQuery(id+"F23.wireOp",EDGE,"E113"),sQuery(id+"F28.wireOp",EDGE,"E146"),sQuery(id+"F28.wireOp",EDGE,"E149")])]});
            var Q1;
            Q1=makeQuery(id+"F29.opExtrude","SWEPT_EDGE",EDGE,{"disambiguationData":[OSD([sQuery(id+"F28.wireOp",EDGE,"E145"),sQuery(id+"F28.wireOp",EDGE,"E149")])]});
            var Q2;
            Q2=makeQuery(id+"F29.opExtrude","SWEPT_EDGE",EDGE,{"disambiguationData":[OSD([sQuery(id+"F23.wireOp",EDGE,"E113"),sQuery(id+"F28.wireOp",EDGE,"E146"),sQuery(id+"F28.wireOp",EDGE,"E150")])]});
            var Q3;
            Q3=makeQuery(id+"F29.opExtrude","SWEPT_EDGE",EDGE,{"disambiguationData":[OSD([sQuery(id+"F28.wireOp",EDGE,"E145"),sQuery(id+"F28.wireOp",EDGE,"E150")])]});
            var Q4;
            Q4=makeQuery(id+"F29.opExtrude","SWEPT_EDGE",EDGE,{"disambiguationData":[OSD([sQuery(id+"F23.wireOp",EDGE,"E113"),sQuery(id+"F28.wireOp",EDGE,"E129"),sQuery(id+"F28.wireOp",EDGE,"E138")])]});
            var Q5;
            Q5=makeQuery(id+"F29.opExtrude","SWEPT_EDGE",EDGE,{"disambiguationData":[OSD([sQuery(id+"F28.wireOp",EDGE,"E132"),sQuery(id+"F28.wireOp",EDGE,"E138")])]});
            var Q6;
            Q6=makeQuery(id+"F29.opExtrude","SWEPT_EDGE",EDGE,{"disambiguationData":[OSD([sQuery(id+"F23.wireOp",EDGE,"E113"),sQuery(id+"F28.wireOp",EDGE,"E129"),sQuery(id+"F28.wireOp",EDGE,"E137")])]});
            var Q7;
            Q7=makeQuery(id+"F29.opExtrude","SWEPT_EDGE",EDGE,{"disambiguationData":[OSD([sQuery(id+"F28.wireOp",EDGE,"E143"),sQuery(id+"F28.wireOp",EDGE,"E151")])]});
            var Q8;
            Q8=makeQuery(id+"F29.opExtrude","SWEPT_EDGE",EDGE,{"disambiguationData":[OSD([sQuery(id+"F28.wireOp",EDGE,"E132"),sQuery(id+"F28.wireOp",EDGE,"E137")])]});
            var Q9;
            Q9=makeQuery(id+"F29.opExtrude","SWEPT_EDGE",EDGE,{"disambiguationData":[OSD([sQuery(id+"F28.wireOp",EDGE,"E133"),sQuery(id+"F28.wireOp",EDGE,"E139")])]});
            var Q10;
            Q10=makeQuery(id+"F29.opExtrude","SWEPT_EDGE",EDGE,{"disambiguationData":[OSD([sQuery(id+"F23.wireOp",EDGE,"E113"),sQuery(id+"F28.wireOp",EDGE,"E144"),sQuery(id+"F28.wireOp",EDGE,"E152")])]});
            var Q11;
            Q11=makeQuery(id+"F29.opExtrude","SWEPT_EDGE",EDGE,{"disambiguationData":[OSD([sQuery(id+"F28.wireOp",EDGE,"E133"),sQuery(id+"F28.wireOp",EDGE,"E140")])]});
            var Q12;
            Q12=makeQuery(id+"F29.opExtrude","SWEPT_EDGE",EDGE,{"disambiguationData":[OSD([sQuery(id+"F23.wireOp",EDGE,"E113"),sQuery(id+"F28.wireOp",EDGE,"E136"),sQuery(id+"F28.wireOp",EDGE,"E140")])]});
            var Q13;
            Q13=makeQuery(id+"F29.opExtrude","SWEPT_EDGE",EDGE,{"disambiguationData":[OSD([sQuery(id+"F28.wireOp",EDGE,"E143"),sQuery(id+"F28.wireOp",EDGE,"E152")])]});
            var Q14;
            Q14=makeQuery(id+"F29.opExtrude","SWEPT_EDGE",EDGE,{"disambiguationData":[OSD([sQuery(id+"F23.wireOp",EDGE,"E113"),sQuery(id+"F28.wireOp",EDGE,"E136"),sQuery(id+"F28.wireOp",EDGE,"E139")])]});
            var Q15;
            Q15=makeQuery(id+"F9CcIupZvPesqnZ_4.opExtrude","CAP_EDGE",EDGE,{"disambiguationData":[OSD([sQuery(id+"F27.wireOp",EDGE,"E119.top")])],"isStart":true});
            var Q16;
            Q16=makeQuery(id+"F9CcIupZvPesqnZ_4.opExtrude","CAP_EDGE",EDGE,{"disambiguationData":[OSD([sQuery(id+"F27.wireOp",EDGE,"E119.left")])],"isStart":true});
            var Q17;
            Q17=makeQuery(id+"F9CcIupZvPesqnZ_4.opExtrude","CAP_EDGE",EDGE,{"disambiguationData":[OSD([sQuery(id+"F27.wireOp",EDGE,"E119.right")])],"isStart":true});
            var Q18;
            Q18=makeQuery(id+"F9CcIupZvPesqnZ_4.opExtrude","CAP_EDGE",EDGE,{"disambiguationData":[OSD([sQuery(id+"F27.wireOp",EDGE,"E118.bottom")])],"isStart":true});
            var Q19;
            Q19=makeQuery(id+"F9CcIupZvPesqnZ_4.opExtrude","CAP_EDGE",EDGE,{"disambiguationData":[OSD([sQuery(id+"F27.wireOp",EDGE,"E118.right")])],"isStart":true});
            var Q20;
            Q20=makeQuery(id+"F9CcIupZvPesqnZ_4.opExtrude","CAP_EDGE",EDGE,{"disambiguationData":[OSD([sQuery(id+"F27.wireOp",EDGE,"E118.left")])],"isStart":true});
            var Q21;
            Q21=makeQuery(id+"FTdqqJJ1uaoRHuZ_4.boolean.opBoolean","COPY",EDGE,{"derivedFrom":makeQuery(id+"FTdqqJJ1uaoRHuZ_4.opExtrude","CAP_EDGE",EDGE,{"disambiguationData":[OSD([sQuery(id+"FRstoslxKUlpYfS_4.wireOp",EDGE,"NezGoiiS-aYT4-GAeU-ITZW-Vp81R6vTZ9WE")])],"isStart":true})});
            var Q22;
            Q22=makeQuery(id+"FbMhszmMvsPUCB8_4.boolean.opBoolean","COPY",EDGE,{"derivedFrom":makeQuery(id+"FbMhszmMvsPUCB8_4.opExtrude","CAP_EDGE",EDGE,{"disambiguationData":[OSD([sQuery(id+"FipGp7p7evltkC6_4.wireOp",EDGE,"wkVAbJIZ-Wn6U-QkLl-WT0G-faB8G608tSpa")])],"isStart":true})});
            var Q23;
            Q23=makeQuery(id+"F29.opExtrude","SWEPT_EDGE",EDGE,{"disambiguationData":[OSD([sQuery(id+"F23.wireOp",EDGE,"E113"),sQuery(id+"F28.wireOp",EDGE,"E144"),sQuery(id+"F28.wireOp",EDGE,"E151")])]});
            var Q24;
            Q24=makeQuery(id+"F9CcIupZvPesqnZ_4.opExtrude","SWEPT_EDGE",EDGE,{"disambiguationData":[OSD([sQuery(id+"F27.wireOp",EDGE,"E118.bottom"),sQuery(id+"F27.wireOp",EDGE,"E118.right")])]});
            var Q25;
            Q25=makeQuery(id+"F9CcIupZvPesqnZ_4.opExtrude","SWEPT_EDGE",EDGE,{"disambiguationData":[OSD([sQuery(id+"F27.wireOp",EDGE,"E118.bottom"),sQuery(id+"F27.wireOp",EDGE,"E118.left")])]});
            var Q26;
            Q26=makeQuery(id+"F9CcIupZvPesqnZ_4.opExtrude","SWEPT_EDGE",EDGE,{"disambiguationData":[OSD([sQuery(id+"F27.wireOp",EDGE,"E119.top"),sQuery(id+"F27.wireOp",EDGE,"E119.left")])]});
            var Q27;
            Q27=makeQuery(id+"F9CcIupZvPesqnZ_4.opExtrude","SWEPT_EDGE",EDGE,{"disambiguationData":[OSD([sQuery(id+"F27.wireOp",EDGE,"E119.top"),sQuery(id+"F27.wireOp",EDGE,"E119.right")])]});
            var Q28;
            Q28=makeQuery(id+"F9CcIupZvPesqnZ_4.opExtrude","TWEAK_EDGE",EDGE,{"derivedFrom":[makeQuery(id+"F16.opExtrude","SWEPT_FACE",FACE,{"disambiguationData":[OSD([sQuery(id+"F15.wireOp",EDGE,"E91")])]}),makeQuery(id+"F27.imprint","IMPRINT",EDGE,{"derivedFrom":sQuery(id+"F27.wireOp",EDGE,"E118.bottom")})]});
            var Q29;
            Q29=makeQuery(id+"F9CcIupZvPesqnZ_4.opExtrude","TWEAK_EDGE",EDGE,{"derivedFrom":[makeQuery(id+"F16.opExtrude","SWEPT_FACE",FACE,{"disambiguationData":[OSD([sQuery(id+"F15.wireOp",EDGE,"E91")])]}),makeQuery(id+"F27.imprint","IMPRINT",EDGE,{"derivedFrom":sQuery(id+"F27.wireOp",EDGE,"E118.left")})]});
            var Q30;
            Q30=makeQuery(id+"F9CcIupZvPesqnZ_4.opExtrude","TWEAK_EDGE",EDGE,{"derivedFrom":[makeQuery(id+"F16.opExtrude","SWEPT_FACE",FACE,{"disambiguationData":[OSD([sQuery(id+"F15.wireOp",EDGE,"E91")])]}),makeQuery(id+"F27.imprint","IMPRINT",EDGE,{"derivedFrom":sQuery(id+"F27.wireOp",EDGE,"E118.right")})]});
            var Q31;
            Q31=makeQuery(id+"F9CcIupZvPesqnZ_4.opExtrude","TWEAK_EDGE",EDGE,{"derivedFrom":[makeQuery(id+"F16.opExtrude","SWEPT_FACE",FACE,{"disambiguationData":[OSD([sQuery(id+"F15.wireOp",EDGE,"E91")])]}),makeQuery(id+"F27.imprint","IMPRINT",EDGE,{"derivedFrom":sQuery(id+"F27.wireOp",EDGE,"E119.left")})]});
            var Q32;
            Q32=makeQuery(id+"F9CcIupZvPesqnZ_4.opExtrude","TWEAK_EDGE",EDGE,{"derivedFrom":[makeQuery(id+"F16.opExtrude","SWEPT_FACE",FACE,{"disambiguationData":[OSD([sQuery(id+"F15.wireOp",EDGE,"E91")])]}),makeQuery(id+"F27.imprint","IMPRINT",EDGE,{"derivedFrom":sQuery(id+"F27.wireOp",EDGE,"E119.top")})]});
            var Q33;
            Q33=makeQuery(id+"F9CcIupZvPesqnZ_4.opExtrude","TWEAK_EDGE",EDGE,{"derivedFrom":[makeQuery(id+"F16.opExtrude","SWEPT_FACE",FACE,{"disambiguationData":[OSD([sQuery(id+"F15.wireOp",EDGE,"E91")])]}),makeQuery(id+"F27.imprint","IMPRINT",EDGE,{"derivedFrom":sQuery(id+"F27.wireOp",EDGE,"E119.right")})]});
            fillet(context, id + "F30", {"entities" : qUnion([Q0, Q1, Q2, Q3, Q4, Q5, Q6, Q7, Q8, Q9, Q10, Q11, Q12, Q13, Q14, Q15, Q16, Q17, Q18, Q19, Q20, Q21, Q22, Q23, Q24, Q25, Q26, Q27, Q28, Q29, Q30, Q31, Q32, Q33]), "radius" : 0.5 * mm, "tangentPropagation" : true, "allowEdgeOverflow" : false});
        }
        {
            var Q0;
            Q0=makeQuery(id+"F24.opExtrude","CAP_FACE",FACE,{"disambiguationData":[OSD([sQuery(id+"F23.wireOp",EDGE,"E113")])],"isStart":true});
            var sketch = newSketch(context, id + "F31", { "sketchPlane" : qUnion([Q0])});
            skLineSegment(sketch, "E153", {"start": v(-18.75, 1.27) * mm, "end": v(-11.68, 1.27) * mm});
            skLineSegment(sketch, "E154", {"start": v(18.75, -1.27) * mm, "end": v(11.68, -1.27) * mm});
            skArc(sketch, "E155", {"start": v(18.75, -1.27) * mm, "mid": v(18.8, 0) * mm, "end": v(18.75, 1.27) * mm});
            skArc(sketch, "E156", {"start": v(-18.75, 1.27) * mm, "mid": v(-18.8, 0) * mm, "end": v(-18.75, -1.27) * mm});
            skPoint(sketch, "E157", {"position": v(-18.8, 0) * mm});
            skLineSegment(sketch, "E158.bottom", {"start": v(-11.68, -7.62) * mm, "end": v(11.68, -7.62) * mm});
            skLineSegment(sketch, "E158.top", {"start": v(-11.68, 7.62) * mm, "end": v(11.68, 7.62) * mm});
            skLineSegment(sketch, "E158.left", {"start": v(-11.68, -7.62) * mm, "end": v(-11.68, -1.27) * mm});
            skLineSegment(sketch, "E158.right", {"start": v(11.68, -7.62) * mm, "end": v(11.68, -1.27) * mm});
            skLineSegment(sketch, "E159", {"start": v(11.68, -1.27) * mm, "end": v(11.68, 1.27) * mm, "construction": true});
            skLineSegment(sketch, "E160", {"start": v(11.68, 1.27) * mm, "end": v(11.68, 7.62) * mm});
            skLineSegment(sketch, "E161", {"start": v(11.68, 1.27) * mm, "end": v(18.75, 1.27) * mm});
            skLineSegment(sketch, "E162", {"start": v(11.68, -1.27) * mm, "end": v(11.68, -1.27) * mm});
            skLineSegment(sketch, "E163", {"start": v(-11.68, -1.27) * mm, "end": v(-11.68, 1.27) * mm, "construction": true});
            skLineSegment(sketch, "E164", {"start": v(-11.68, -1.27) * mm, "end": v(-18.75, -1.27) * mm});
            skLineSegment(sketch, "E165", {"start": v(-11.68, 1.27) * mm, "end": v(11.68, 1.27) * mm, "construction": true});
            skLineSegment(sketch, "E166", {"start": v(-11.68, 1.27) * mm, "end": v(-11.68, 7.62) * mm});
            skLineSegment(sketch, "E167", {"start": v(11.68, -1.27) * mm, "end": v(-11.68, -1.27) * mm, "construction": true});
            skSolve(sketch);
        }
        {
            var Q0;
            Q0=qSketchRegion(id+"F31",true);
            extrude(context, id + "F32", {"entities" : qUnion([Q0]), "operationType" : NewBodyOperationType.REMOVE, "oppositeDirection" : true, "depth" : 1.02 * mm, "offsetDistance" : 25.4 * mm});
        }
        {
            var Q0;
            Q0=qSketchRegion(id+"F27",true);
            extrude(context, id + "F33", {"entities" : qUnion([Q0]), "operationType" : NewBodyOperationType.ADD, "depth" : 6.35 * mm, "offsetDistance" : 25.4 * mm});
        }
    });
